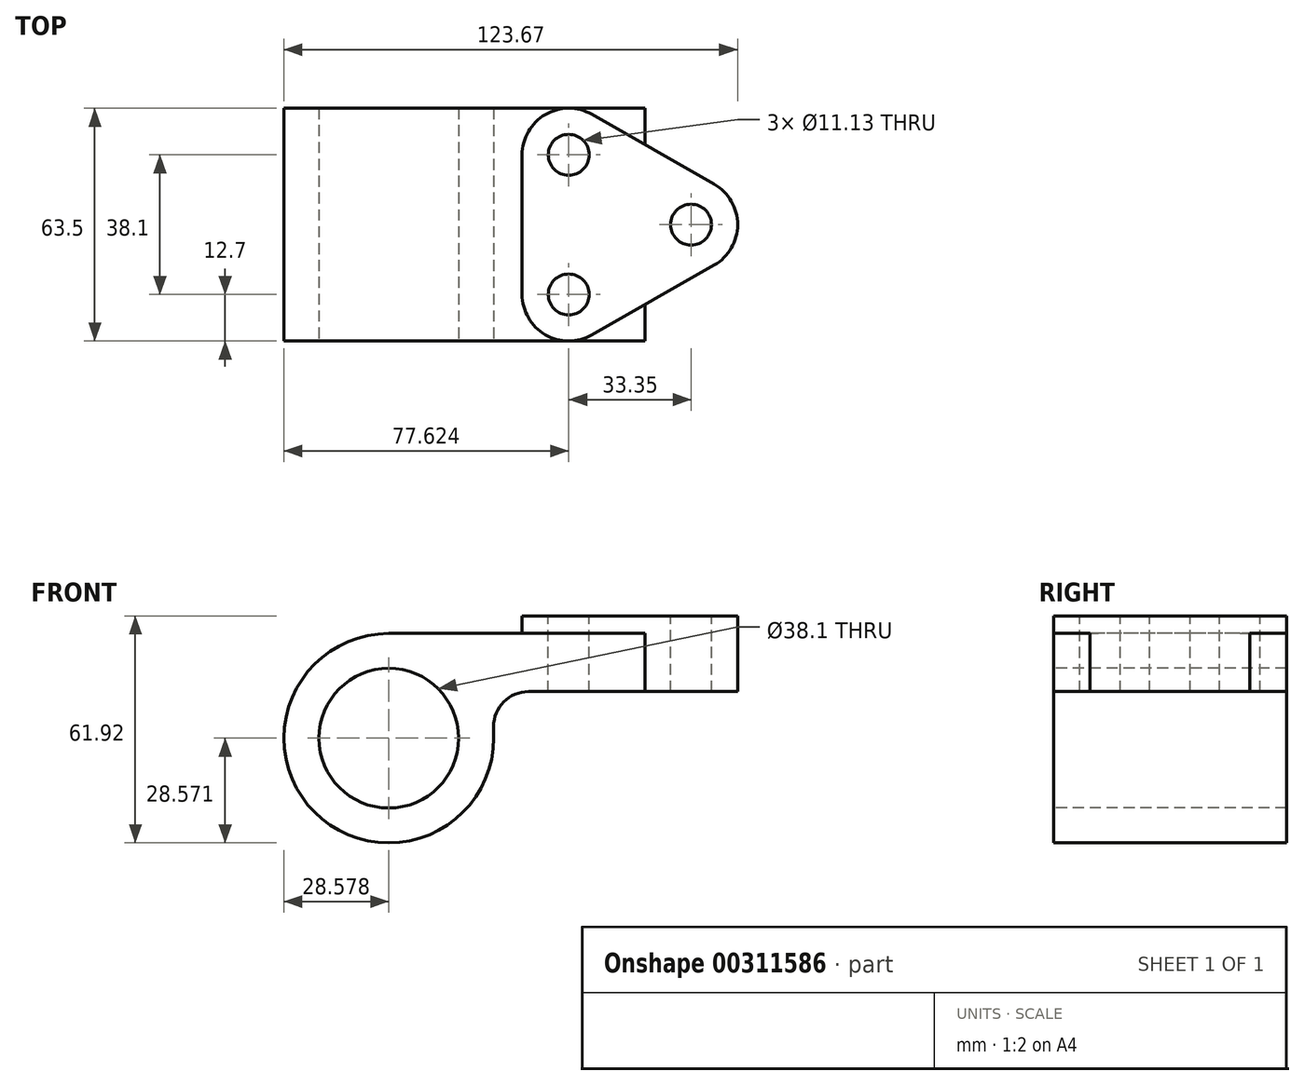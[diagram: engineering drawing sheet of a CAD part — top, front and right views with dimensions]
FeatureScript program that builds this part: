
annotation { "Feature Type Name" : "Feature", "Feature Type Description" : "" }
export const myFeature = defineFeature(function(context is Context, id is Id, definition is map)
    precondition{}
    {
        {
            var Q0;
            Q0=qCreatedBy(makeId("Front.planeOp"),FACE);
            var sketch = newSketch(context, id + "F0", { "sketchPlane" : qUnion([Q0])});
            skCircle(sketch, "E0", {"center": v(-27.5, 33.75) * mm, "radius": 28.58 * mm});
            skCircle(sketch, "E1", {"center": v(-27.5, 33.75) * mm, "radius": 19.05 * mm});
            skLineSegment(sketch, "E2", {"start": v(-27.5, 62.33) * mm, "end": v(42.36, 62.33) * mm});
            skLineSegment(sketch, "E3", {"start": v(42.36, 62.33) * mm, "end": v(42.36, 46.45) * mm});
            skLineSegment(sketch, "E4", {"start": v(1.08, 33.75) * mm, "end": v(1.08, 46.45) * mm});
            skLineSegment(sketch, "E5", {"start": v(1.08, 46.45) * mm, "end": v(42.36, 46.45) * mm});
            skSolve(sketch);
        }
        {
            var Q0;
            Q0 = qSketchRegion(id + "F0", true);
            extrude(context, id + "F1", {"entities" : qUnion([Q0]), "endBound" : BoundingType.SYMMETRIC, "oppositeDirection" : true, "depth" : 63.5 * mm});
        }
        {
            var Q0;
            Q0=makeQuery(id+"F1.opExtrude","SWEPT_EDGE",EDGE,{"disambiguationData":[OSD([sQuery(id+"F0.wireOp",EDGE,"E4"),sQuery(id+"F0.wireOp",EDGE,"E5")])]});
            fillet(context, id + "F2", {"entities" : qUnion([Q0]), "radius" : 9.52 * mm, "tangentPropagation" : true, "allowEdgeOverflow" : false});
        }
        {
            var Q0;
            Q0=makeQuery(id+"F1.opExtrude","SWEPT_FACE",FACE,{"disambiguationData":[OSD([sQuery(id+"F0.wireOp",EDGE,"E2")])]});
            var sketch = newSketch(context, id + "F3", { "sketchPlane" : qUnion([Q0])});
            skLineSegment(sketch, "E6", {"start": v(8.85, 19.05) * mm, "end": v(8.85, -19.05) * mm});
            skLineSegment(sketch, "E7", {"start": v(27.85, -30.08) * mm, "end": v(61.2, -11.03) * mm});
            skLineSegment(sketch, "E8", {"start": v(61.2, 11.03) * mm, "end": v(27.85, 30.08) * mm});
            skLineSegment(sketch, "E9", {"start": v(0, 0) * mm, "end": v(80.5, 0) * mm, "construction": true});
            skPoint(sketch, "E10.visualSharp", {"position": v(80.5, 0) * mm});
            skArc(sketch, "E10.filletArc", {"start": v(61.2, -11.03) * mm, "mid": v(67.6, 0) * mm, "end": v(61.2, 11.03) * mm});
            skPoint(sketch, "E11.visualSharp", {"position": v(8.85, 40.93) * mm});
            skArc(sketch, "E11.filletArc", {"start": v(27.85, 30.08) * mm, "mid": v(15.18, 30.03) * mm, "end": v(8.85, 19.05) * mm});
            skPoint(sketch, "E12.visualSharp", {"position": v(8.85, -40.93) * mm});
            skArc(sketch, "E12.filletArc", {"start": v(8.85, -19.05) * mm, "mid": v(15.18, -30.03) * mm, "end": v(27.85, -30.08) * mm});
            skSolve(sketch);
        }
        {
            var Q0;
            Q0 = qSketchRegion(id + "F3", true);
            extrude(context, id + "F4", {"entities" : qUnion([Q0]), "operationType" : NewBodyOperationType.ADD, "depth" : 4.78 * mm, "hasSecondDirection" : true, "secondDirectionOppositeDirection" : true, "secondDirectionDepth" : 15.88 * mm});
        }
        {
            var Q0;
            Q0=makeQuery(id+"F4.opExtrude","CAP_FACE",FACE,{"disambiguationData":[OSD([sQuery(id+"F3.wireOp",EDGE,"E6"),sQuery(id+"F3.wireOp",EDGE,"E7"),sQuery(id+"F3.wireOp",EDGE,"E8"),sQuery(id+"F3.wireOp",EDGE,"E10.filletArc"),sQuery(id+"F3.wireOp",EDGE,"E11.filletArc"),sQuery(id+"F3.wireOp",EDGE,"E12.filletArc")])],"isStart":false});
            var sketch = newSketch(context, id + "F5", { "sketchPlane" : qUnion([Q0])});
            skCircle(sketch, "E13", {"center": v(21.55, 19.05) * mm, "radius": 5.56 * mm});
            skCircle(sketch, "E14", {"center": v(21.55, -19.05) * mm, "radius": 5.56 * mm});
            skCircle(sketch, "E15", {"center": v(54.9, 0) * mm, "radius": 5.56 * mm});
            skSolve(sketch);
        }
        {
            var Q0;
            Q0 = qSketchRegion(id + "F5", true);
            extrude(context, id + "F6", {"entities" : qUnion([Q0]), "operationType" : NewBodyOperationType.REMOVE, "oppositeDirection" : true, "depth" : 25.4 * mm});
        }
    });
